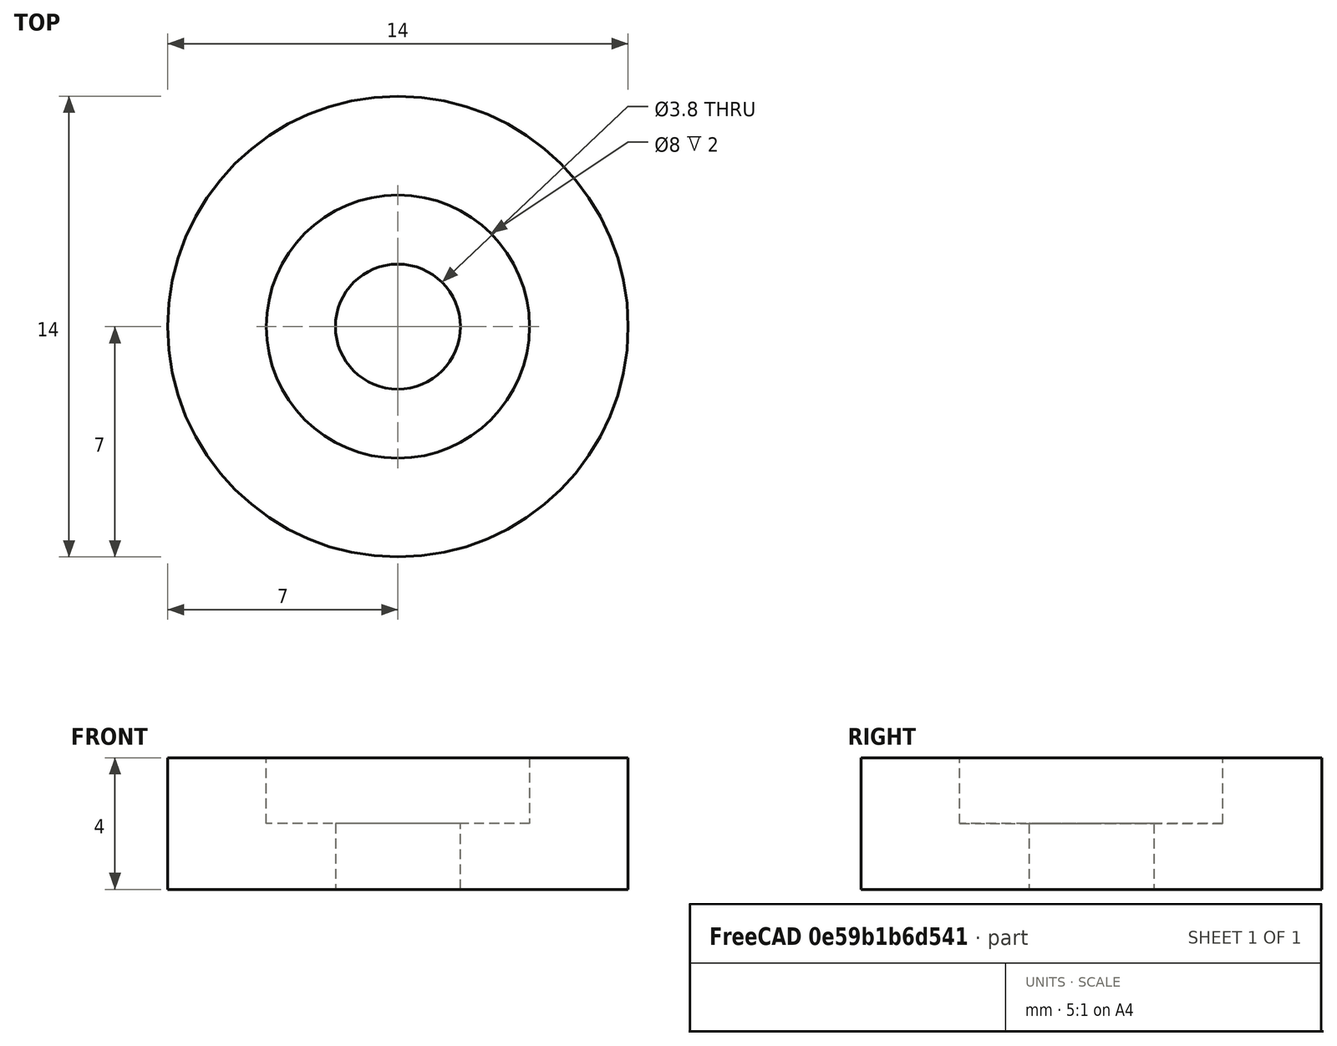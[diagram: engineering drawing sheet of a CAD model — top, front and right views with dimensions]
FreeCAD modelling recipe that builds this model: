
FCSTD DOCUMENT  (FreeCAD 0.17R13662 (Git))
Label: flexy_standoff
License: All rights reserved
LicenseURL: http://en.wikipedia.org/wiki/All_rights_reserved
objects: Sketcher::SketchObject×2, PartDesign::Pad×1, PartDesign::Pocket×1, PartDesign::Body×1
note: 7 computed .brp shape members not serialized (recipe doc carries the construction recipe); baked Part::Feature solids carry a one-line shape summary decoded from their .brp

FEATURE [Sketcher::SketchObject] Sketch
  MapMode = 5
  Support = -> [XY_Plane]
  sketch-geometry (2):
    g0: Circle CenterX=0 CenterY=0 CenterZ=0 NormalX=0 NormalY=0 NormalZ=1 AngleXU=0 Radius=1.9
    g1: Circle CenterX=0 CenterY=0 CenterZ=0 NormalX=0 NormalY=0 NormalZ=1 AngleXU=0 Radius=7
  constraints (3):
    c: Coincident(g0,g-1)
    c: Radius(g0) = 1.9
    c: Radius(g1) = 7
FEATURE [PartDesign::Pad] Pad
  Length = 4
  Length2 = 100
  Profile = -> Sketch
  Type = 0
FEATURE [Sketcher::SketchObject] Sketch001
  MapMode = 5
  Placement = pos=(0,0,4) rot=(0,0,1;0rad)
  Support = -> [Pad]
  sketch-geometry (1):
    g0: Circle CenterX=0 CenterY=0 CenterZ=0 NormalX=0 NormalY=0 NormalZ=1 AngleXU=0 Radius=4
  constraints (1):
    c: Radius(g0) = 4
FEATURE [PartDesign::Pocket] Pocket
  BaseFeature = -> Pad
  Length = 2
  Length2 = 100
  Profile = -> Sketch001
  Type = 0
FEATURE [PartDesign::Body] Body
  Group = -> [Sketch,Pad,Sketch001,Pocket]
  Origin = -> Origin
  Tip = -> Pocket
